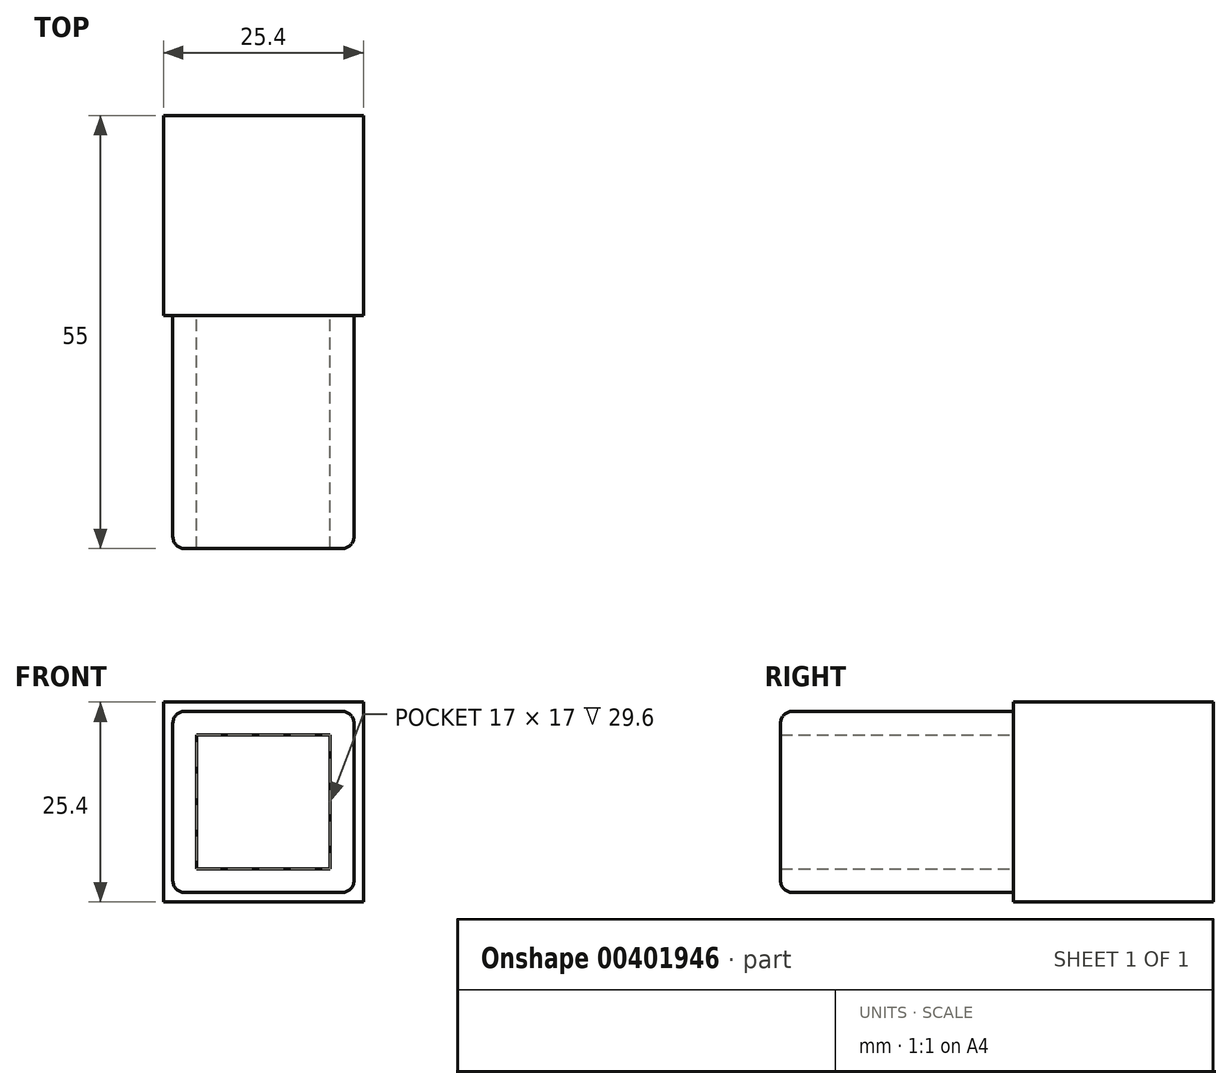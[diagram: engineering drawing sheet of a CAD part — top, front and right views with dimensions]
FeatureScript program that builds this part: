
annotation { "Feature Type Name" : "Feature", "Feature Type Description" : "" }
export const myFeature = defineFeature(function(context is Context, id is Id, definition is map)
    precondition{}
    {
        {
            var Q0;
            Q0=qCreatedBy(makeId("Front.planeOp"),FACE);
            var sketch = newSketch(context, id + "F0", { "sketchPlane" : qUnion([Q0])});
            skLineSegment(sketch, "E0.bottom", {"start": v(-12.7, 12.7) * mm, "end": v(12.7, 12.7) * mm});
            skLineSegment(sketch, "E0.top", {"start": v(-12.7, -12.7) * mm, "end": v(12.7, -12.7) * mm});
            skLineSegment(sketch, "E0.left", {"start": v(-12.7, 12.7) * mm, "end": v(-12.7, -12.7) * mm});
            skLineSegment(sketch, "E0.right", {"start": v(12.7, 12.7) * mm, "end": v(12.7, -12.7) * mm});
            skLineSegment(sketch, "E1", {"start": v(-12.7, 0) * mm, "end": v(0, 0) * mm, "construction": true});
            skLineSegment(sketch, "E2", {"start": v(0, 0) * mm, "end": v(0, 12.7) * mm, "construction": true});
            skSolve(sketch);
        }
        {
            var Q0;
            Q0=makeQuery(id+"F0.imprint","IMPRINT",FACE,{"disambiguationData":[TD([[makeQuery(id+"F0.imprint","IMPRINT",EDGE,{"derivedFrom":sQuery(id+"F0.wireOp",EDGE,"E0.bottom")}),-1.0]])]});
            extrude(context, id + "F1", {"entities" : qUnion([Q0]), "endBound" : BoundingType.SYMMETRIC, "depth" : 25.4 * mm});
        }
        {
            var Q0;
            Q0=makeQuery(id+"F1.opExtrude","CAP_FACE",FACE,{"disambiguationData":[OSD([sQuery(id+"F0.wireOp",EDGE,"E0.bottom"),sQuery(id+"F0.wireOp",EDGE,"E0.top"),sQuery(id+"F0.wireOp",EDGE,"E0.left"),sQuery(id+"F0.wireOp",EDGE,"E0.right")])],"isStart":false});
            var sketch = newSketch(context, id + "F2", { "sketchPlane" : qUnion([Q0])});
            skLineSegment(sketch, "E3.0", {"start": v(-11.5, 11.5) * mm, "end": v(-11.5, -11.5) * mm});
            skLineSegment(sketch, "E3.1", {"start": v(11.5, 11.5) * mm, "end": v(-11.5, 11.5) * mm});
            skLineSegment(sketch, "E3.2", {"start": v(11.5, -11.5) * mm, "end": v(11.5, 11.5) * mm});
            skLineSegment(sketch, "E3.3", {"start": v(-11.5, -11.5) * mm, "end": v(11.5, -11.5) * mm});
            skLineSegment(sketch, "E4.0.1", {"start": v(-12.7, -12.7) * mm, "end": v(12.7, -12.7) * mm});
            skLineSegment(sketch, "E5.0", {"start": v(8.5, 8.5) * mm, "end": v(-8.5, 8.5) * mm});
            skLineSegment(sketch, "E5.1", {"start": v(8.5, -8.5) * mm, "end": v(8.5, 8.5) * mm});
            skLineSegment(sketch, "E5.2", {"start": v(-8.5, -8.5) * mm, "end": v(8.5, -8.5) * mm});
            skLineSegment(sketch, "E5.3", {"start": v(-8.5, 8.5) * mm, "end": v(-8.5, -8.5) * mm});
            skSolve(sketch);
        }
        {
            var Q0;
            Q0=qSketchRegion(id+"F2",true);
            extrude(context, id + "F3", {"entities" : qUnion([Q0]), "operationType" : NewBodyOperationType.ADD, "depth" : (55 - 25.4) * mm});
        }
        {
            var Q0;
            Q0=makeQuery(id+"F3.opExtrude","SWEPT_EDGE",EDGE,{"disambiguationData":[OSD([sQuery(id+"F2.wireOp",EDGE,"E3.1"),sQuery(id+"F2.wireOp",EDGE,"E3.2")])]});
            var Q1;
            Q1=makeQuery(id+"F3.opExtrude","SWEPT_EDGE",EDGE,{"disambiguationData":[OSD([sQuery(id+"F2.wireOp",EDGE,"E3.2"),sQuery(id+"F2.wireOp",EDGE,"E3.3")])]});
            var Q2;
            Q2=makeQuery(id+"F3.opExtrude","SWEPT_EDGE",EDGE,{"disambiguationData":[OSD([sQuery(id+"F2.wireOp",EDGE,"E3.0"),sQuery(id+"F2.wireOp",EDGE,"E3.1")])]});
            var Q3;
            Q3=makeQuery(id+"F3.opExtrude","SWEPT_EDGE",EDGE,{"disambiguationData":[OSD([sQuery(id+"F2.wireOp",EDGE,"E3.0"),sQuery(id+"F2.wireOp",EDGE,"E3.3")])]});
            var Q4;
            Q4=makeQuery(id+"F3.opExtrude","CAP_EDGE",EDGE,{"disambiguationData":[OSD([sQuery(id+"F2.wireOp",EDGE,"E3.1")])],"isStart":false});
            var Q5;
            Q5=makeQuery(id+"F3.opExtrude","CAP_EDGE",EDGE,{"disambiguationData":[OSD([sQuery(id+"F2.wireOp",EDGE,"E3.2")])],"isStart":false});
            var Q6;
            Q6=makeQuery(id+"F3.opExtrude","CAP_EDGE",EDGE,{"disambiguationData":[OSD([sQuery(id+"F2.wireOp",EDGE,"E3.3")])],"isStart":false});
            var Q7;
            Q7=makeQuery(id+"F3.opExtrude","CAP_EDGE",EDGE,{"disambiguationData":[OSD([sQuery(id+"F2.wireOp",EDGE,"E3.0")])],"isStart":false});
            fillet(context, id + "F4", {"entities" : qUnion([Q0, Q1, Q2, Q3, Q4, Q5, Q6, Q7]), "radius" : 1.5 * mm, "tangentPropagation" : true, "allowEdgeOverflow" : false});
        }
        {
            var Q0;
            Q0=qCreatedBy(makeId("Front.planeOp"),FACE);
            var sketch = newSketch(context, id + "F5", { "sketchPlane" : qUnion([Q0])});
            skLineSegment(sketch, "E6", {"start": v(0, 70.28) * mm, "end": v(0, -12.35) * mm, "construction": true});
            skLineSegment(sketch, "E7", {"start": v(-37.45, 0) * mm, "end": v(15.14, 0) * mm, "construction": true});
            skSolve(sketch);
        }
    });
